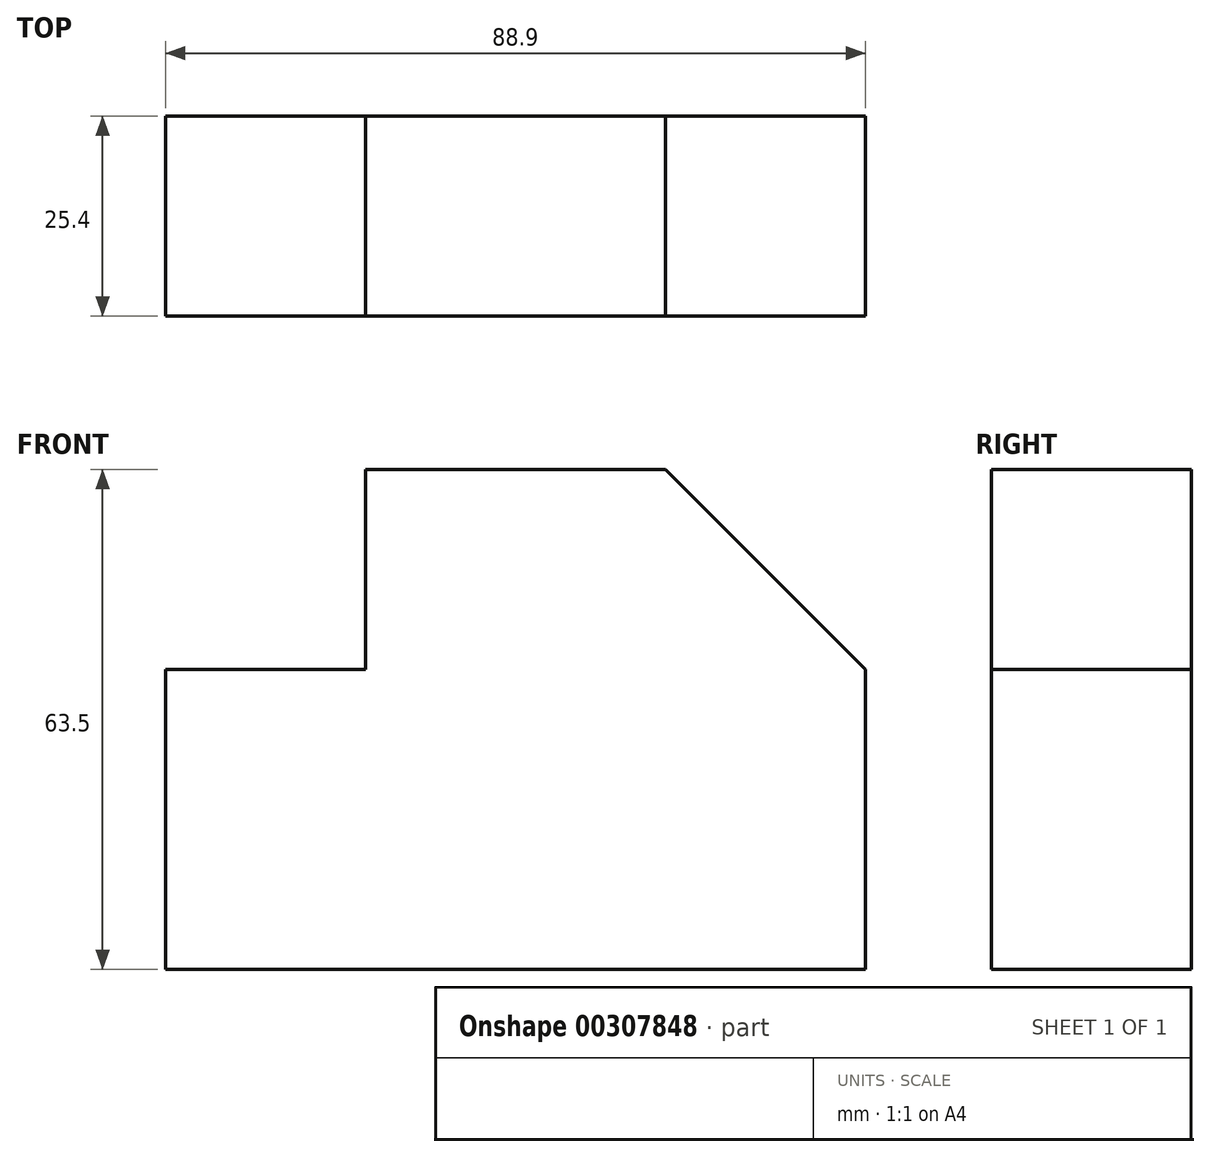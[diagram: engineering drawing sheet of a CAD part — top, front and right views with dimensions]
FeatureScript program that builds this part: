
annotation { "Feature Type Name" : "Feature", "Feature Type Description" : "" }
export const myFeature = defineFeature(function(context is Context, id is Id, definition is map)
    precondition{}
    {
        {
            var Q0;
            Q0=qCreatedBy(makeId("Front.planeOp"),FACE);
            var sketch = newSketch(context, id + "F0", { "sketchPlane" : qUnion([Q0])});
            skLineSegment(sketch, "E0", {"start": v(-50.89, -60.76) * mm, "end": v(38.01, -60.76) * mm});
            skLineSegment(sketch, "E1", {"start": v(38.01, -60.76) * mm, "end": v(38.01, -22.66) * mm});
            skLineSegment(sketch, "E2", {"start": v(38.01, -22.66) * mm, "end": v(12.61, 2.74) * mm});
            skLineSegment(sketch, "E3", {"start": v(12.61, 2.74) * mm, "end": v(-25.49, 2.74) * mm});
            skLineSegment(sketch, "E4", {"start": v(-25.49, 2.74) * mm, "end": v(-25.49, -22.66) * mm});
            skLineSegment(sketch, "E5", {"start": v(-25.49, -22.66) * mm, "end": v(-50.89, -22.66) * mm});
            skLineSegment(sketch, "E6", {"start": v(-50.89, -22.66) * mm, "end": v(-50.89, -60.76) * mm});
            skSolve(sketch);
        }
        {
            var Q0;
            Q0=makeQuery(id+"F0.imprint","IMPRINT",FACE,{"disambiguationData":[TD([[makeQuery(id+"F0.imprint","IMPRINT",EDGE,{"derivedFrom":sQuery(id+"F0.wireOp",EDGE,"E0")}),1.0]])]});
            extrude(context, id + "F1", {"entities" : qUnion([Q0]), "depth" : 25.4 * mm});
        }
    });
